# Revit family: BCHH
name_source: partatom
category: Air Terminals
revit_build: Autodesk Revit MEP 2012 (Build: 20110309_2315(x64)
units: mm (PartAtom-declared; Revit-internal decimal feet)

## types (4) — shared parameters
Altura = 1 7/8"
Manufacturer = INNE
Máxima presión estática = 0.00 in-wg
Máxima velocidad de cuello = 0 FPM
Mínima presión estática = 0.00 in-wg
Mínima velocidad de cuello = 0 FPM
Travesaño medio = Yes
Travesaños laterales = No
URL = http://www.inne.com.mx
prueba = 1/4"
separación = 3/4"

## per-type parameters (varying)
| type | A Largo | B Alto | B marco | Height | No. de elementos | N° de rejillas | Width |
| BCHH-20-12 | 19 3/4" | 11 3/4" | 13 13/32" | 13 1/4" | 26 | 16 | 21 1/4" |
| BCHH-22-14 | 21 3/4" | 13 3/4" | 15 13/32" | 15 1/4" | 29 | 18 | 23 1/4" |
| BCHH-24-16 | 23 3/4" | 15 3/4" | 17 13/32" | 17 1/4" | 32 | 21 | 25 1/4" |
| BCHH-26-18 | 25 3/4" | 17 3/4" | 19 13/32" | 19 1/4" | 34 | 24 | 27 1/4" |

## geometry (parser evidence)
native form markers: Sweep x5
no freeform markers — native parametric forms only
